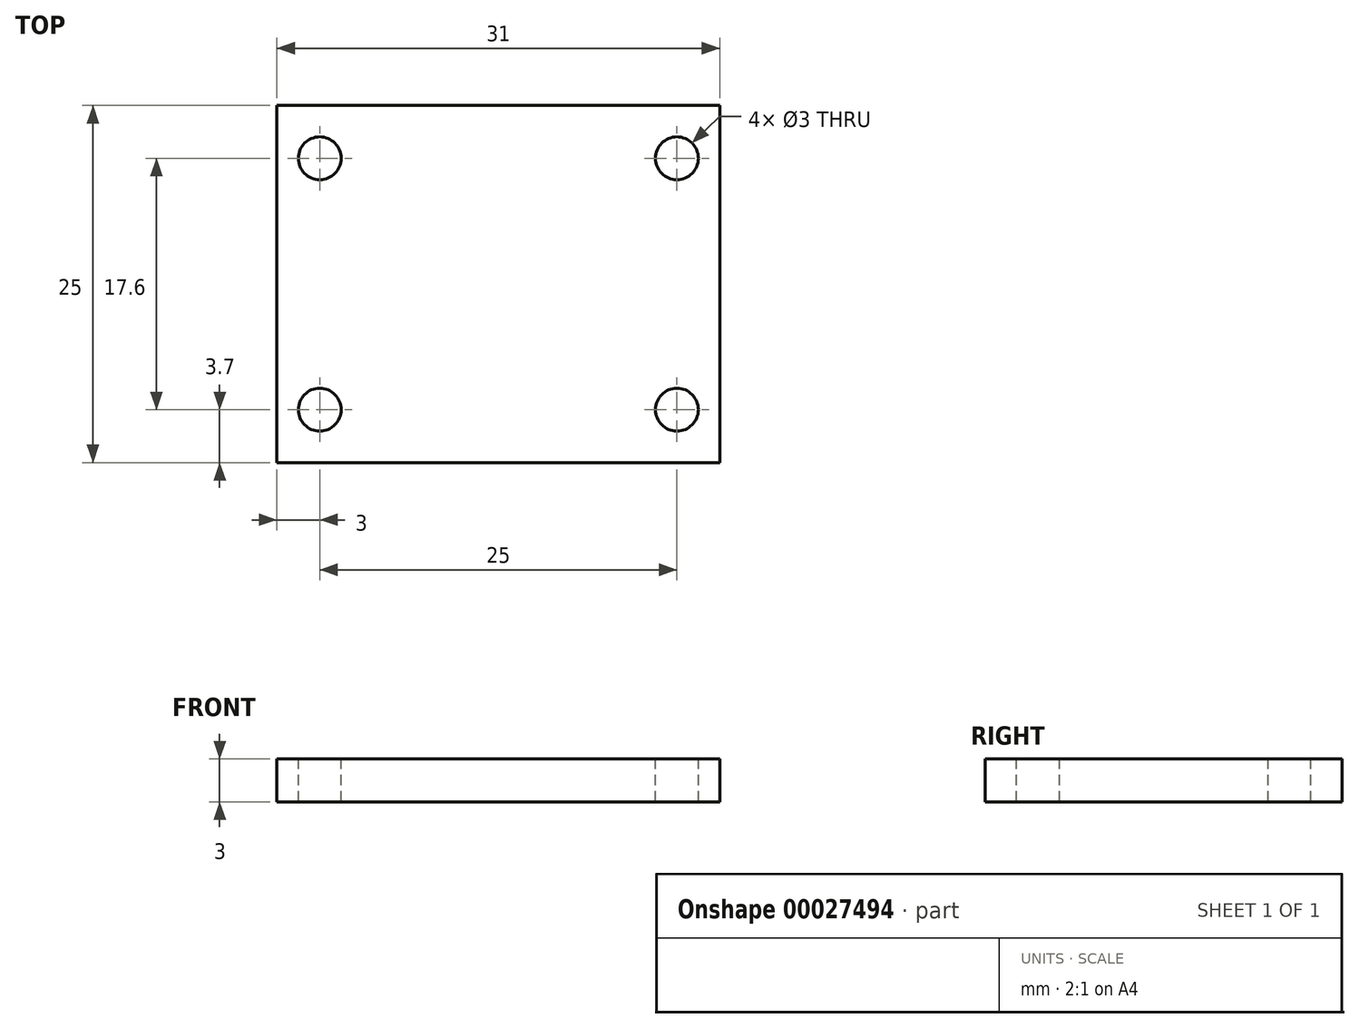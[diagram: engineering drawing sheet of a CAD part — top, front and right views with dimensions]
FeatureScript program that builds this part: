
annotation { "Feature Type Name" : "Feature", "Feature Type Description" : "" }
export const myFeature = defineFeature(function(context is Context, id is Id, definition is map)
    precondition{}
    {
        {
            var Q0;
            Q0=qCreatedBy(makeId("Top.planeOp"),FACE);
            var sketch = newSketch(context, id + "F0", { "sketchPlane" : qUnion([Q0])});
            skLineSegment(sketch, "E0.rect.bottom", {"start": v(15.5, 12.5) * mm, "end": v(-15.5, 12.5) * mm});
            skLineSegment(sketch, "E0.rect.top", {"start": v(15.5, -12.5) * mm, "end": v(-15.5, -12.5) * mm});
            skLineSegment(sketch, "E0.rect.left", {"start": v(15.5, 12.5) * mm, "end": v(15.5, -12.5) * mm});
            skLineSegment(sketch, "E0.rect.right", {"start": v(-15.5, 12.5) * mm, "end": v(-15.5, -12.5) * mm});
            skPoint(sketch, "E0.rect.middle", {"position": v(0, 0) * mm});
            skSolve(sketch);
        }
        {
            var Q0;
            Q0=makeQuery(id+"F0.imprint","IMPRINT",FACE,{"disambiguationData":[TD([[makeQuery(id+"F0.imprint","IMPRINT",EDGE,{"derivedFrom":sQuery(id+"F0.wireOp",EDGE,"E0.rect.bottom")}),1.0]])]});
            extrude(context, id + "F1", {"entities" : qUnion([Q0]), "depth" : 3 * mm});
        }
        {
            var Q0;
            Q0=makeQuery(id+"F1.opExtrude","CAP_FACE",FACE,{"disambiguationData":[OSD([sQuery(id+"F0.wireOp",EDGE,"E0.rect.bottom"),sQuery(id+"F0.wireOp",EDGE,"E0.rect.top"),sQuery(id+"F0.wireOp",EDGE,"E0.rect.left"),sQuery(id+"F0.wireOp",EDGE,"E0.rect.right")])],"isStart":false});
            var sketch = newSketch(context, id + "F2", { "sketchPlane" : qUnion([Q0])});
            skLineSegment(sketch, "E1", {"start": v(-15.5, 5.1) * mm, "end": v(15.5, 5.1) * mm, "construction": true});
            skLineSegment(sketch, "E2", {"start": v(15.5, -5.1) * mm, "end": v(-15.5, -5.1) * mm, "construction": true});
            skLineSegment(sketch, "E3", {"start": v(-15.5, 8.8) * mm, "end": v(15.5, 8.8) * mm, "construction": true});
            skLineSegment(sketch, "E4", {"start": v(15.5, -8.8) * mm, "end": v(-15.5, -8.8) * mm, "construction": true});
            skCircle(sketch, "E5", {"center": v(-12.5, 8.8) * mm, "radius": 1.5 * mm});
            skLineSegment(sketch, "E6", {"start": v(-15.5, 0) * mm, "end": v(15.5, 0) * mm, "construction": true});
            skCircle(sketch, "E7.MirrorC", {"center": v(-12.5, -8.8) * mm, "radius": 1.5 * mm});
            skLineSegment(sketch, "E8", {"start": v(0, 12.5) * mm, "end": v(0, -12.5) * mm, "construction": true});
            skCircle(sketch, "E9.MirrorC", {"center": v(12.5, 8.8) * mm, "radius": 1.5 * mm});
            skCircle(sketch, "E10.MirrorC", {"center": v(12.5, -8.8) * mm, "radius": 1.5 * mm});
            skSolve(sketch);
        }
        {
            var Q0;
            Q0=qSketchRegion(id+"F2",true);
            extrude(context, id + "F3", {"entities" : qUnion([Q0]), "operationType" : NewBodyOperationType.REMOVE, "oppositeDirection" : true, "depth" : 25 * mm});
        }
    });
